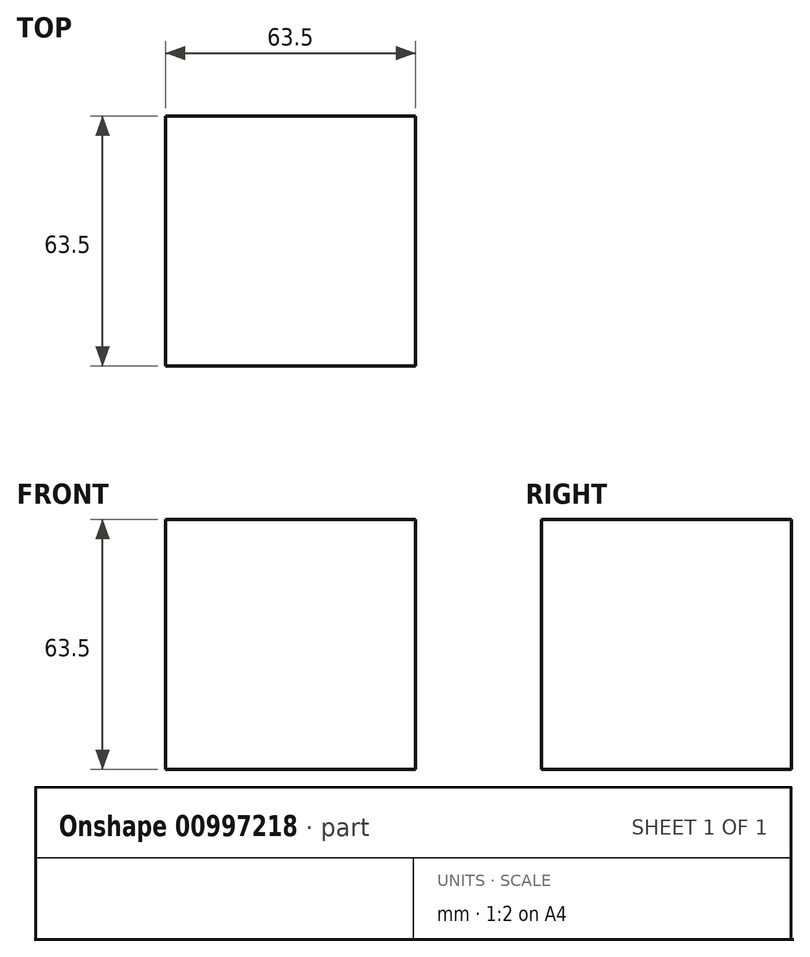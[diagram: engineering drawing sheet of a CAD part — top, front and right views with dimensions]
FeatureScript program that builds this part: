
annotation { "Feature Type Name" : "Feature", "Feature Type Description" : "" }
export const myFeature = defineFeature(function(context is Context, id is Id, definition is map)
    precondition{}
    {
        {
            var Q0;
            Q0=qCreatedBy(makeId("Top.planeOp"),FACE);
            var sketch = newSketch(context, id + "F0", { "sketchPlane" : qUnion([Q0])});
            skLineSegment(sketch, "E0.bottom", {"start": v(-31.75, 31.75) * mm, "end": v(31.75, 31.75) * mm});
            skLineSegment(sketch, "E0.top", {"start": v(-31.75, -31.75) * mm, "end": v(31.75, -31.75) * mm});
            skLineSegment(sketch, "E0.left", {"start": v(-31.75, 31.75) * mm, "end": v(-31.75, -31.75) * mm});
            skLineSegment(sketch, "E0.right", {"start": v(31.75, 31.75) * mm, "end": v(31.75, -31.75) * mm});
            skPoint(sketch, "E0.middle", {"position": v(0, 0) * mm});
            skSolve(sketch);
        }
        {
            var Q0;
            Q0=makeQuery(id+"F0.imprint","IMPRINT",FACE,{"disambiguationData":[TD([[makeQuery(id+"F0.imprint","IMPRINT",EDGE,{"derivedFrom":sQuery(id+"F0.wireOp",EDGE,"E0.bottom")}),-1.0]])]});
            extrude(context, id + "F1", {"entities" : qUnion([Q0]), "depth" : 63.5 * mm, "offsetDistance" : 25.4 * mm});
        }
    });
